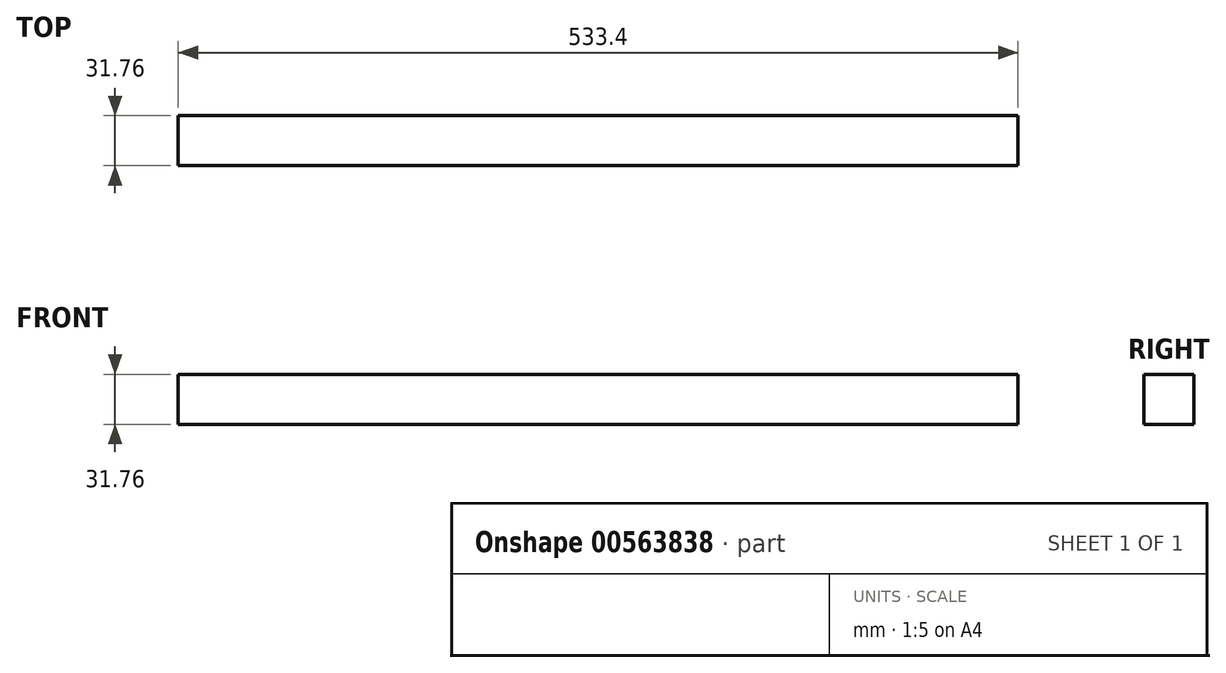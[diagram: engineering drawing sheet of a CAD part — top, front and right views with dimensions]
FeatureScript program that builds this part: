
annotation { "Feature Type Name" : "Feature", "Feature Type Description" : "" }
export const myFeature = defineFeature(function(context is Context, id is Id, definition is map)
    precondition{}
    {
        {
            var Q0;
            Q0=qCreatedBy(makeId("Front.planeOp"),FACE);
            var sketch = newSketch(context, id + "F0", { "sketchPlane" : qUnion([Q0])});
            skLineSegment(sketch, "E0.bottom", {"start": v(-266.7, 15.88) * mm, "end": v(266.7, 15.88) * mm});
            skLineSegment(sketch, "E0.top", {"start": v(-266.7, -15.88) * mm, "end": v(266.7, -15.88) * mm});
            skLineSegment(sketch, "E0.left", {"start": v(-266.7, 15.88) * mm, "end": v(-266.7, -15.88) * mm});
            skLineSegment(sketch, "E0.right", {"start": v(266.7, 15.88) * mm, "end": v(266.7, -15.88) * mm});
            skPoint(sketch, "E0.middle", {"position": v(0, 0) * mm});
            skSolve(sketch);
        }
        {
            var Q0;
            Q0=makeQuery(id+"F0.imprint","IMPRINT",FACE,{"disambiguationData":[TD([[makeQuery(id+"F0.imprint","IMPRINT",EDGE,{"derivedFrom":sQuery(id+"F0.wireOp",EDGE,"E0.bottom")}),-1.0]])]});
            extrude(context, id + "F1", {"entities" : qUnion([Q0]), "endBound" : BoundingType.SYMMETRIC, "depth" : 31.75 * mm, "offsetDistance" : 25.4 * mm});
        }
    });
